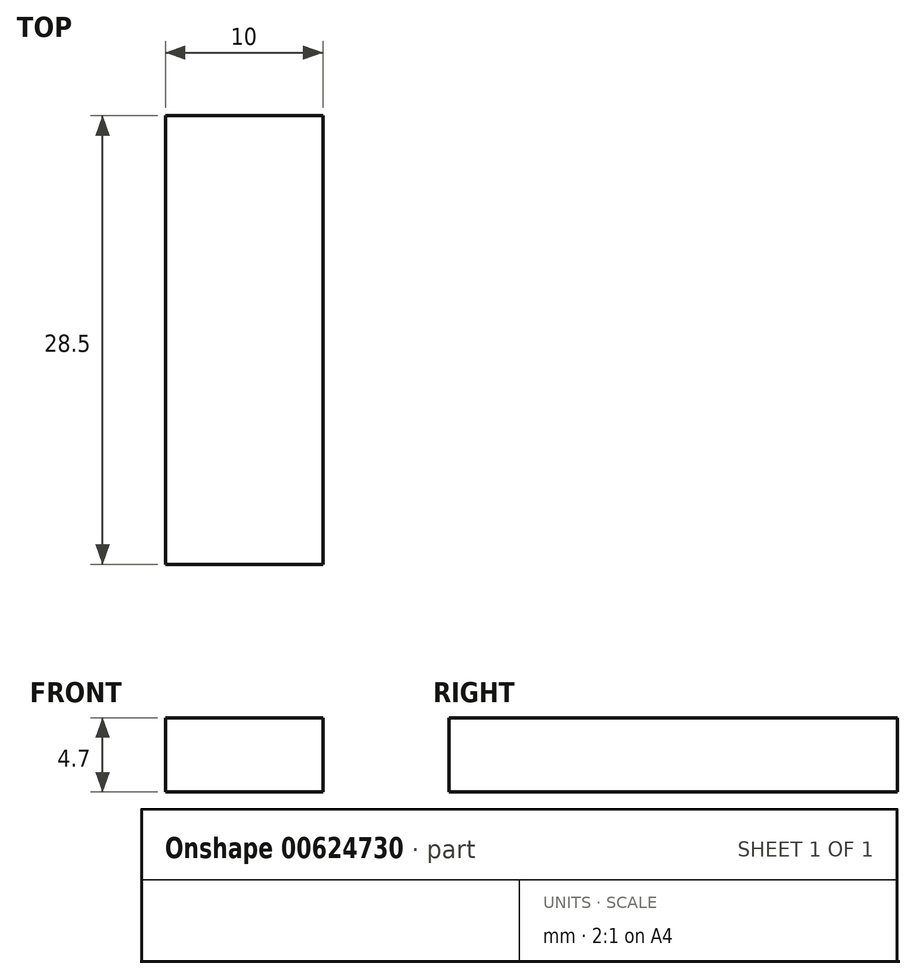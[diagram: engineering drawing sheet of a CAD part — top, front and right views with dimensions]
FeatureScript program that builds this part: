
annotation { "Feature Type Name" : "Feature", "Feature Type Description" : "" }
export const myFeature = defineFeature(function(context is Context, id is Id, definition is map)
    precondition{}
    {
        {
            var Q0;
            Q0=qCreatedBy(makeId("Front.planeOp"),FACE);
            var sketch = newSketch(context, id + "F0", { "sketchPlane" : qUnion([Q0])});
            skLineSegment(sketch, "E0.bottom", {"start": v(-5, 0) * mm, "end": v(5, 0) * mm});
            skLineSegment(sketch, "E0.top", {"start": v(-5, 4.7) * mm, "end": v(5, 4.7) * mm});
            skLineSegment(sketch, "E0.left", {"start": v(-5, 0) * mm, "end": v(-5, 4.7) * mm});
            skLineSegment(sketch, "E0.right", {"start": v(5, 0) * mm, "end": v(5, 4.7) * mm});
            skSolve(sketch);
        }
        {
            var Q0;
            Q0 = qSketchRegion(id + "F0", true);
            extrude(context, id + "F1", {"entities" : qUnion([Q0]), "depth" : 28.5 * mm, "offsetDistance" : 25 * mm});
        }
    });
